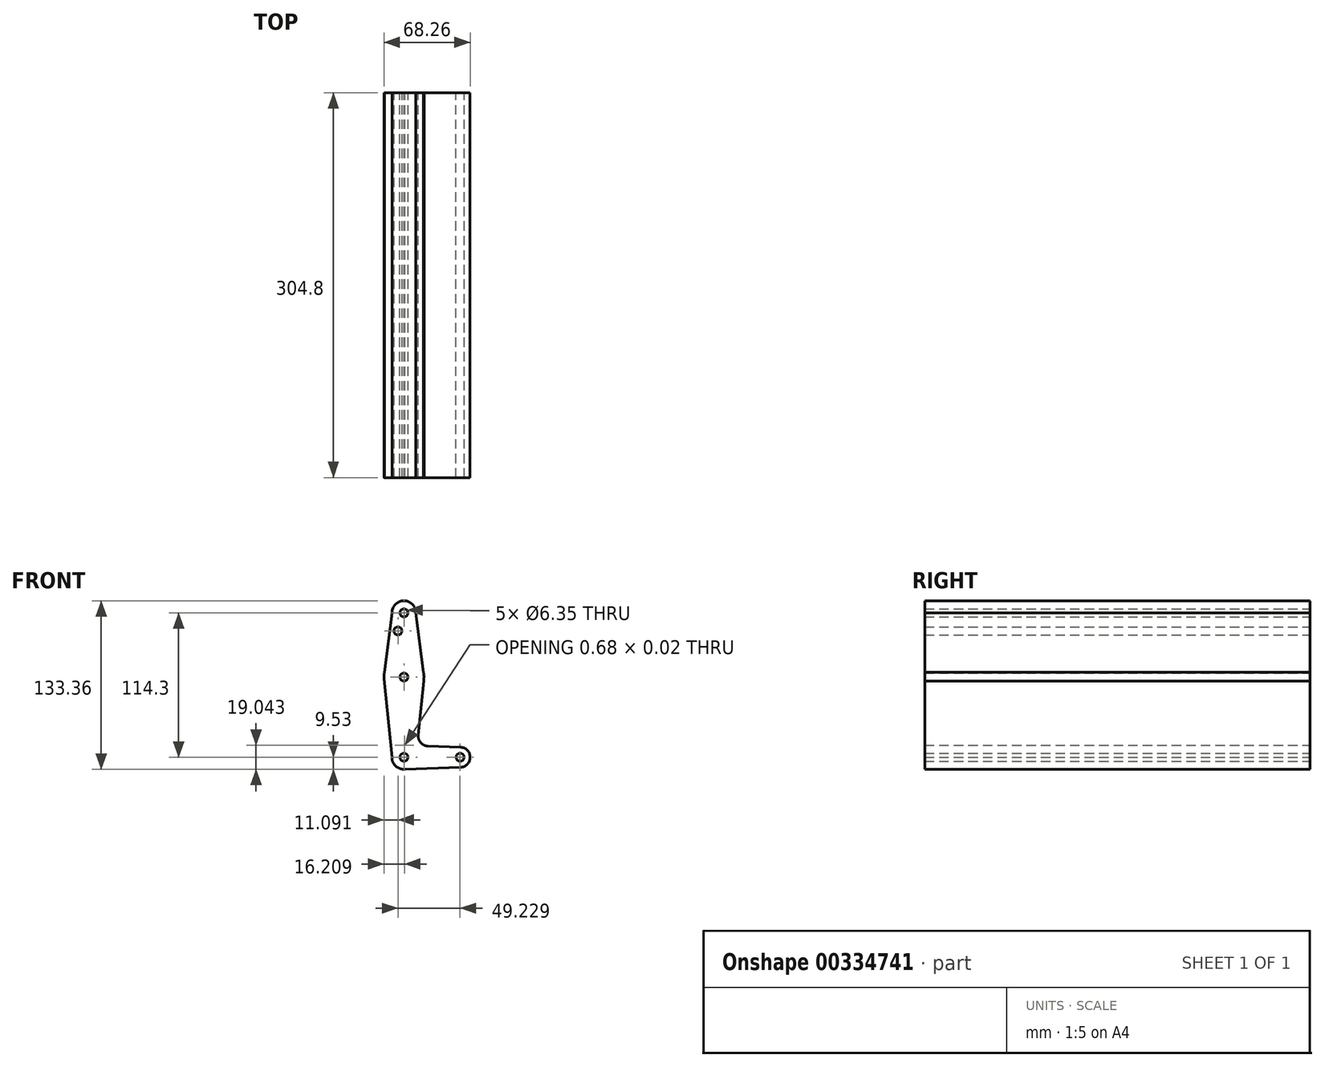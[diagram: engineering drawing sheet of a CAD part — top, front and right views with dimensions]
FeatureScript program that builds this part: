
annotation { "Feature Type Name" : "Feature", "Feature Type Description" : "" }
export const myFeature = defineFeature(function(context is Context, id is Id, definition is map)
    precondition{}
    {
        {
            var Q0;
            Q0=qCreatedBy(makeId("Front.planeOp"),FACE);
            var sketch = newSketch(context, id + "F0", { "sketchPlane" : qUnion([Q0])});
            skLineSegment(sketch, "E0", {"start": v(0, 114.3) * mm, "end": v(0, 0) * mm, "construction": true});
            skLineSegment(sketch, "E1", {"start": v(0, 0) * mm, "end": v(44.45, 0) * mm, "construction": true});
            skCircle(sketch, "E2", {"center": v(0, 0) * mm, "radius": 9.53 * mm});
            skCircle(sketch, "E3", {"center": v(44.45, 0) * mm, "radius": 7.94 * mm});
            skCircle(sketch, "E4", {"center": v(0, 114.3) * mm, "radius": 9.53 * mm});
            skLineSegment(sketch, "E5", {"start": v(0, 9.53) * mm, "end": v(44.73, 7.93) * mm});
            skCircle(sketch, "E6", {"center": v(0, 63.5) * mm, "radius": 15.88 * mm});
            skLineSegment(sketch, "E7", {"start": v(18.95, 8.85) * mm, "end": v(44.73, 7.93) * mm});
            skLineSegment(sketch, "E8", {"start": v(0, -9.53) * mm, "end": v(44.73, -7.93) * mm});
            skLineSegment(sketch, "E9", {"start": v(9.52, 114.3) * mm, "end": v(15.88, 63.5) * mm});
            skLineSegment(sketch, "E10", {"start": v(-9.53, 114.3) * mm, "end": v(-15.87, 63.5) * mm});
            skCircle(sketch, "E11", {"center": v(0, 114.3) * mm, "radius": 3.18 * mm});
            skCircle(sketch, "E12", {"center": v(-4.78, 100.03) * mm, "radius": 3.18 * mm});
            skCircle(sketch, "E13", {"center": v(0, 63.5) * mm, "radius": 3.18 * mm});
            skCircle(sketch, "E14", {"center": v(0, 0) * mm, "radius": 3.18 * mm});
            skCircle(sketch, "E15", {"center": v(44.45, 0) * mm, "radius": 3.18 * mm});
            skLineSegment(sketch, "E16", {"start": v(15.88, 63.5) * mm, "end": v(11.32, 17.58) * mm});
            skLineSegment(sketch, "E17", {"start": v(-15.8, 61.9) * mm, "end": v(-9.52, 0) * mm});
            skPoint(sketch, "E18.newPointA", {"position": v(9.57, 0) * mm});
            skArc(sketch, "E18.filletArc", {"start": v(11.32, 17.58) * mm, "mid": v(13.24, 11.56) * mm, "end": v(18.95, 8.85) * mm});
            skSolve(sketch);
        }
        {
            var Q0;
            Q0 = qSketchRegion(id + "F0", true);
            extrude(context, id + "F1", {"entities" : qUnion([Q0]), "depth" : 304.8 * mm});
        }
    });
